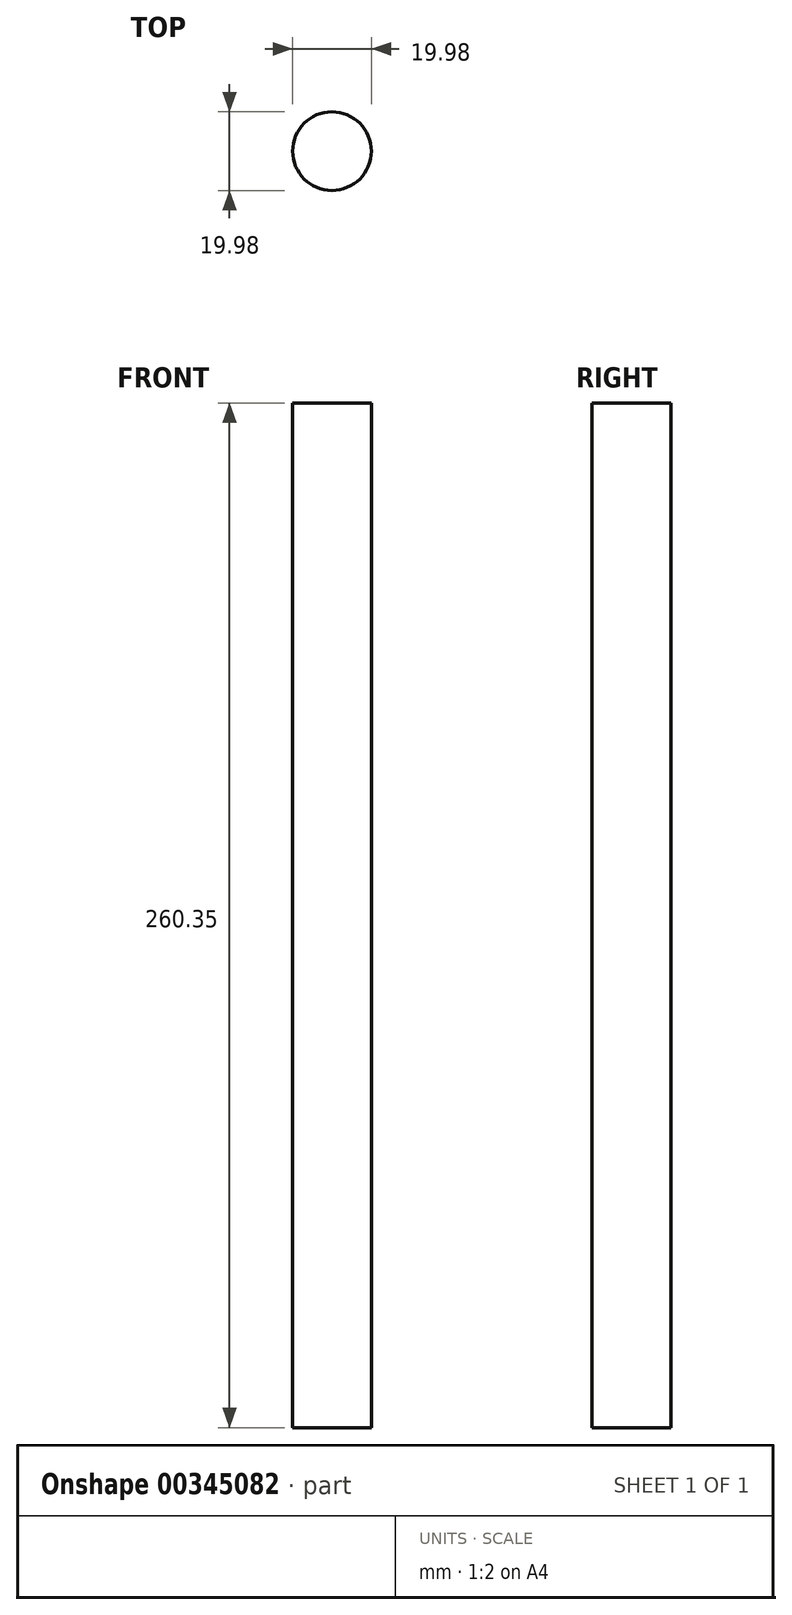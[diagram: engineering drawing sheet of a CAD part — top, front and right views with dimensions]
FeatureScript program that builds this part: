
annotation { "Feature Type Name" : "Feature", "Feature Type Description" : "" }
export const myFeature = defineFeature(function(context is Context, id is Id, definition is map)
    precondition{}
    {
        {
            var Q0;
            Q0=qCreatedBy(makeId("Top.planeOp"),FACE);
            var sketch = newSketch(context, id + "F0", { "sketchPlane" : qUnion([Q0])});
            skCircle(sketch, "E0", {"center": v(0, 0) * mm, "radius": 10 * mm});
            skSolve(sketch);
        }
        {
            var Q0;
            Q0=makeQuery(id+"F0.imprint","IMPRINT",FACE,{"disambiguationData":[TD([[makeQuery(id+"F0.imprint","IMPRINT",EDGE,{"derivedFrom":sQuery(id+"F0.wireOp",EDGE,"E0")}),1.0]])]});
            var Q1;
            Q1=sQuery(id+"F0.wireOp",EDGE,"E0");
            extrude(context, id + "F1", {"entities" : qUnion([Q0]), "surfaceEntities" : qUnion([Q1]), "oppositeDirection" : true, "depth" : 260.35 * mm});
        }
    });
